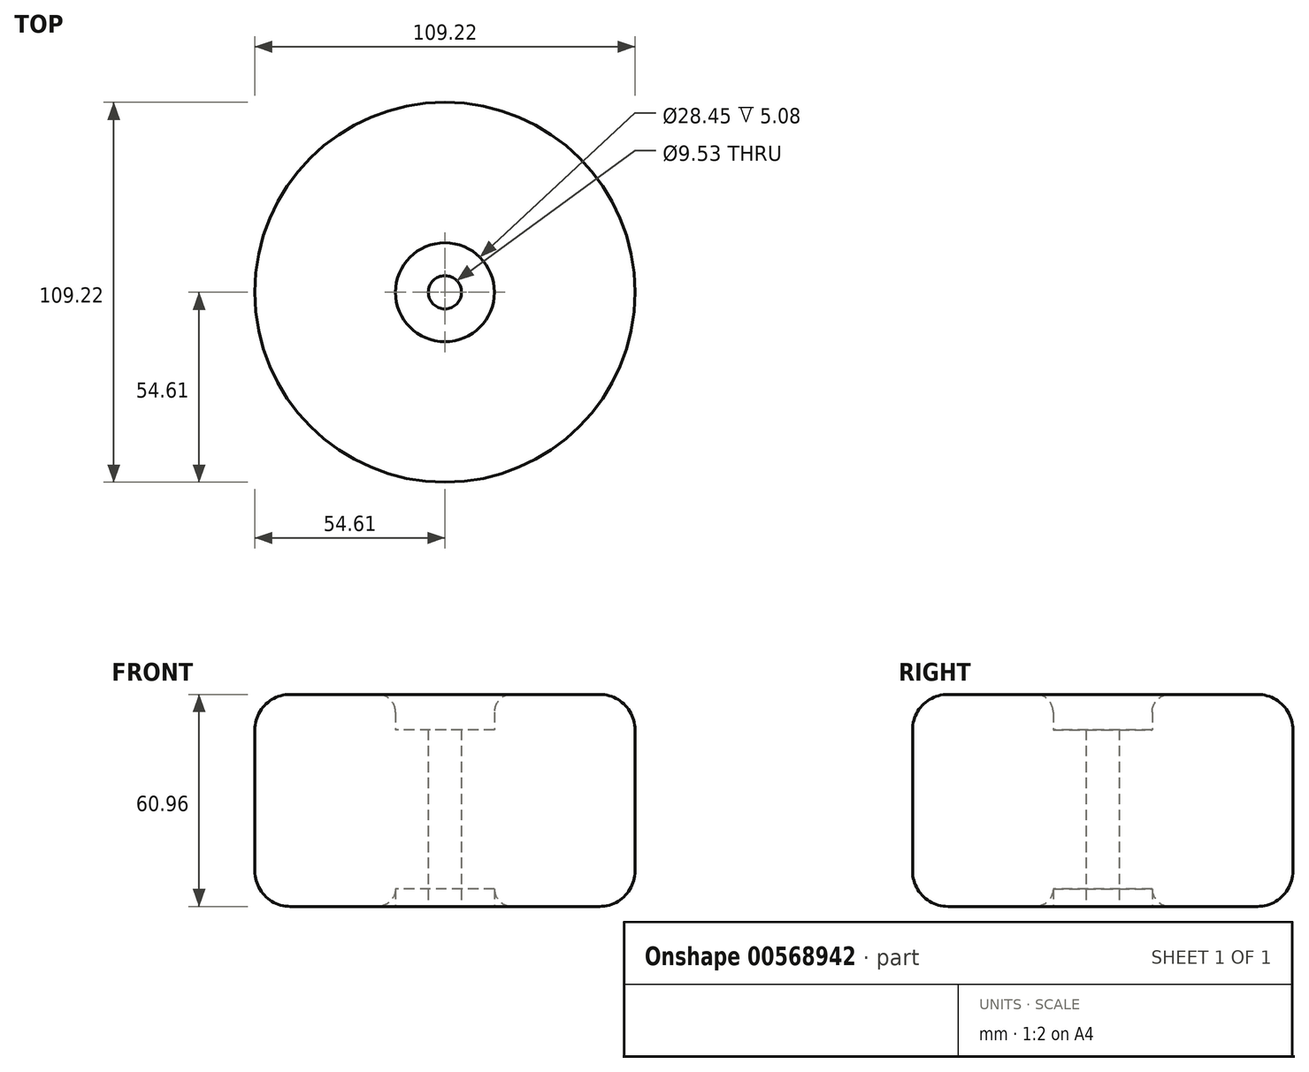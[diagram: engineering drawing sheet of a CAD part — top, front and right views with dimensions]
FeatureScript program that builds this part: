
annotation { "Feature Type Name" : "Feature", "Feature Type Description" : "" }
export const myFeature = defineFeature(function(context is Context, id is Id, definition is map)
    precondition{}
    {
        {
            var Q0;
            Q0=qCreatedBy(makeId("Top.planeOp"),FACE);
            var sketch = newSketch(context, id + "F0", { "sketchPlane" : qUnion([Q0])});
            skCircle(sketch, "E0", {"center": v(0, 0) * mm, "radius": 54.61 * mm});
            skCircle(sketch, "E1", {"center": v(0, 0) * mm, "radius": 14.22 * mm});
            skCircle(sketch, "E2", {"center": v(0, 0) * mm, "radius": 4.76 * mm});
            skSolve(sketch);
        }
        {
            var Q0;
            Q0 = qSketchRegion(id + "F0", true);
            extrude(context, id + "F1", {"entities" : qUnion([Q0]), "depth" : 60.96 * mm, "offsetDistance" : 25.4 * mm});
        }
        {
            var Q0;
            Q0=makeQuery(id+"F1.opExtrude","CAP_EDGE",EDGE,{"disambiguationData":[OSD([sQuery(id+"F0.wireOp",EDGE,"E0")])],"isStart":true});
            var Q1;
            Q1=makeQuery(id+"F1.opExtrude","CAP_EDGE",EDGE,{"disambiguationData":[OSD([sQuery(id+"F0.wireOp",EDGE,"E0")])],"isStart":false});
            fillet(context, id + "F2", {"entities" : qUnion([Q0, Q1]), "radius" : 10.16 * mm, "tangentPropagation" : true, "allowEdgeOverflow" : false});
        }
        {
            var Q0;
            Q0=makeQuery(id+"F1.opExtrude","CAP_EDGE",EDGE,{"disambiguationData":[OSD([sQuery(id+"F0.wireOp",EDGE,"E1")])],"isStart":false});
            var Q1;
            Q1=makeQuery(id+"F1.opExtrude","CAP_EDGE",EDGE,{"disambiguationData":[OSD([sQuery(id+"F0.wireOp",EDGE,"E1")])],"isStart":true});
            fillet(context, id + "F3", {"entities" : qUnion([Q0, Q1]), "radius" : 5.08 * mm, "tangentPropagation" : true, "allowEdgeOverflow" : false});
        }
        {
            var Q0;
            Q0=makeQuery(id+"F0.imprint","IMPRINT",FACE,{"disambiguationData":[TD([[makeQuery(id+"F0.imprint","IMPRINT",EDGE,{"derivedFrom":sQuery(id+"F0.wireOp",EDGE,"E1")}),1.0]])]});
            extrude(context, id + "F4", {"entities" : qUnion([Q0]), "operationType" : NewBodyOperationType.ADD, "depth" : 50.8 * mm, "offsetDistance" : 25.4 * mm});
        }
    });
